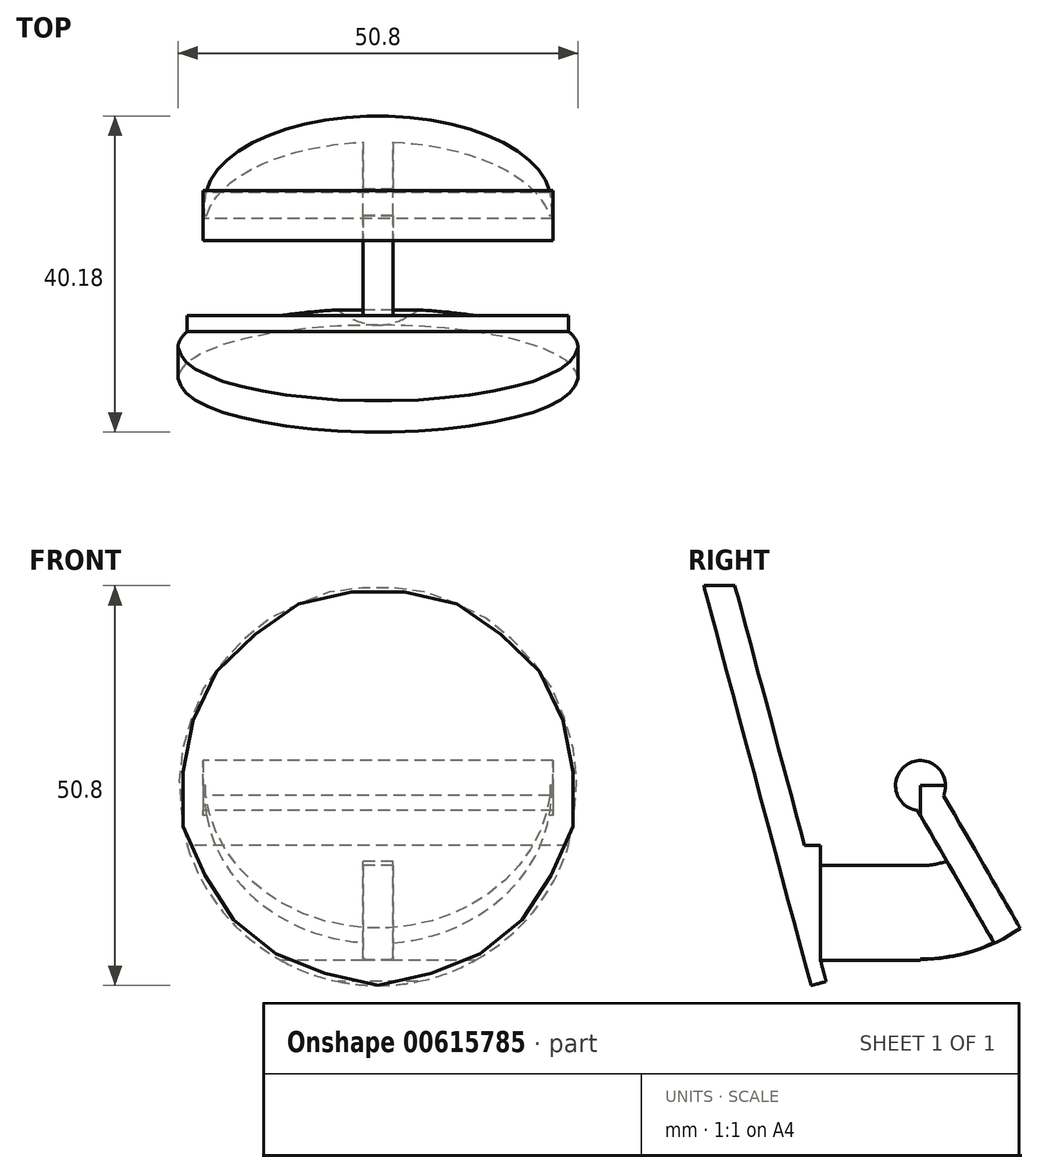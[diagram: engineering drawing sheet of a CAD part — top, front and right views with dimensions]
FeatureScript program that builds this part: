
annotation { "Feature Type Name" : "Feature", "Feature Type Description" : "" }
export const myFeature = defineFeature(function(context is Context, id is Id, definition is map)
    precondition{}
    {
        {
            var Q0;
            Q0=qCreatedBy(makeId("Right.planeOp"),FACE);
            var sketch = newSketch(context, id + "F0", { "sketchPlane" : qUnion([Q0])});
            skCircle(sketch, "E0", {"center": v(0, 0) * mm, "radius": 3.17 * mm});
            skLineSegment(sketch, "E1", {"start": v(2.92, -1.25) * mm, "end": v(28.32, -45.24) * mm});
            skLineSegment(sketch, "E2", {"start": v(28.32, -45.24) * mm, "end": v(25.02, -47.15) * mm});
            skLineSegment(sketch, "E3", {"start": v(25.02, -47.15) * mm, "end": v(-0.38, -3.15) * mm});
            skLineSegment(sketch, "E4", {"start": v(0, 0) * mm, "end": v(3.28, -5.69) * mm, "construction": true});
            skSolve(sketch);
        }
        {
            var Q0;
            Q0 = qSketchRegion(id + "F0", true);
            extrude(context, id + "F1", {"entities" : qUnion([Q0]), "endBound" : BoundingType.SYMMETRIC, "depth" : 44.45 * mm, "offsetDistance" : 25.4 * mm});
        }
        {
            var Q0;
            Q0=qCreatedBy(makeId("Right.planeOp"),FACE);
            var sketch = newSketch(context, id + "F2", { "sketchPlane" : qUnion([Q0])});
            skArc(sketch, "E5", {"start": v(4.9, -8.9) * mm, "mid": v(2.53, -9.84) * mm, "end": v(0, -10.16) * mm});
            skLineSegment(sketch, "E6", {"start": v(-12.7, 0) * mm, "end": v(-12.7, -23.65) * mm, "construction": true});
            skLineSegment(sketch, "E7", {"start": v(0, -10.16) * mm, "end": v(-12.7, -10.16) * mm});
            skLineSegment(sketch, "E8", {"start": v(-12.7, -10.16) * mm, "end": v(-12.7, -53.34) * mm});
            skLineSegment(sketch, "E9", {"start": v(-12.7, -53.34) * mm, "end": v(0, -53.34) * mm});
            skArc(sketch, "E10", {"start": v(0, -53.34) * mm, "mid": v(13.7, -51.55) * mm, "end": v(26.5, -46.3) * mm});
            skLineSegment(sketch, "E11", {"start": v(4.9, -8.9) * mm, "end": v(26.5, -46.3) * mm});
            skSolve(sketch);
        }
        {
            var Q0;
            Q0 = qSketchRegion(id + "F2", true);
            extrude(context, id + "F3", {"entities" : qUnion([Q0]), "operationType" : NewBodyOperationType.ADD, "endBound" : BoundingType.SYMMETRIC, "depth" : 3.8 * mm, "offsetDistance" : 25.4 * mm});
        }
        {
            var Q0;
            Q0=qCreatedBy(makeId("Right.planeOp"),FACE);
            var sketch = newSketch(context, id + "F4", { "sketchPlane" : qUnion([Q0])});
            skArc(sketch, "E12", {"start": v(0, -22.23) * mm, "mid": v(21.2, 6.66) * mm, "end": v(-12.7, 18.24) * mm});
            skLineSegment(sketch, "E13", {"start": v(0, -22.23) * mm, "end": v(-12.7, -22.23) * mm});
            skLineSegment(sketch, "E14", {"start": v(-12.7, -22.23) * mm, "end": v(-12.7, 18.24) * mm});
            skSolve(sketch);
        }
        {
            var Q0;
            Q0 = qSketchRegion(id + "F4", true);
            extrude(context, id + "F5", {"entities" : qUnion([Q0]), "operationType" : NewBodyOperationType.INTERSECT, "endBound" : BoundingType.SYMMETRIC, "depth" : 76.2 * mm, "offsetDistance" : 25.4 * mm});
        }
        {
            var Q0;
            Q0=qCreatedBy(makeId("Front.planeOp"),FACE);
            var sketch = newSketch(context, id + "F6", { "sketchPlane" : qUnion([Q0])});
            skLineSegment(sketch, "E15", {"start": v(18.5, -7.35) * mm, "end": v(18.5, -7.35) * mm});
            skLineSegment(sketch, "E16", {"start": v(0, 0) * mm, "end": v(22.1, 0) * mm, "construction": true});
            skArc(sketch, "E17", {"start": v(22.1, 0) * mm, "mid": v(0, -22.1) * mm, "end": v(-22.1, 0) * mm});
            skLineSegment(sketch, "E18", {"start": v(-22.1, 0) * mm, "end": v(0, 0) * mm, "construction": true});
            skLineSegment(sketch, "E19", {"start": v(-30.28, 0) * mm, "end": v(-30.28, -27.19) * mm});
            skLineSegment(sketch, "E20", {"start": v(-30.28, -27.19) * mm, "end": v(29.54, -27.19) * mm});
            skLineSegment(sketch, "E21", {"start": v(29.54, -27.19) * mm, "end": v(29.54, 0) * mm});
            skLineSegment(sketch, "E22", {"start": v(29.54, 0) * mm, "end": v(22.1, 0) * mm});
            skLineSegment(sketch, "E23", {"start": v(-22.1, 0) * mm, "end": v(-30.28, 0) * mm});
            skSolve(sketch);
        }
        {
            var Q0;
            Q0 = qSketchRegion(id + "F6", true);
            var Q1;
            Q1=sQuery(id+"F6.wireOp",EDGE,"E16");
            revolve(context, id + "F7", {"operationType" : NewBodyOperationType.REMOVE, "entities" : qUnion([Q0]), "axis" : qUnion([Q1]), "revolveType" : RevolveType.ONE_DIRECTION, "angle" : 90 * degree});
        }
        {
            var Q0;
            Q0=qCreatedBy(makeId("Right.planeOp"),FACE);
            var sketch = newSketch(context, id + "F8", { "sketchPlane" : qUnion([Q0])});
            skLineSegment(sketch, "E24", {"start": v(-27.52, 25.4) * mm, "end": v(-14.76, -22.23) * mm});
            skLineSegment(sketch, "E25", {"start": v(-14.76, -22.23) * mm, "end": v(-12.7, -22.23) * mm});
            skLineSegment(sketch, "E26", {"start": v(-12.7, -22.23) * mm, "end": v(-12.7, -7.62) * mm});
            skLineSegment(sketch, "E27", {"start": v(-12.7, -7.62) * mm, "end": v(-14.73, -7.62) * mm});
            skLineSegment(sketch, "E28", {"start": v(-14.73, -7.62) * mm, "end": v(-23.58, 25.4) * mm});
            skLineSegment(sketch, "E29", {"start": v(-23.58, 25.4) * mm, "end": v(-27.52, 25.4) * mm});
            skLineSegment(sketch, "E30", {"start": v(-14.76, -22.23) * mm, "end": v(-13.91, -25.4) * mm});
            skLineSegment(sketch, "E31", {"start": v(-13.91, -25.4) * mm, "end": v(-11.99, -24.88) * mm});
            skLineSegment(sketch, "E32", {"start": v(-11.99, -24.88) * mm, "end": v(-12.7, -22.23) * mm});
            skSolve(sketch);
        }
        {
            var Q0;
            Q0 = qSketchRegion(id + "F8", true);
            extrude(context, id + "F9", {"entities" : qUnion([Q0]), "operationType" : NewBodyOperationType.ADD, "endBound" : BoundingType.SYMMETRIC, "depth" : 63.5 * mm, "offsetDistance" : 25.4 * mm});
        }
        {
            var Q0;
            Q0=qCreatedBy(makeId("Front.planeOp"),FACE);
            var sketch = newSketch(context, id + "F10", { "sketchPlane" : qUnion([Q0])});
            skCircle(sketch, "E33", {"center": v(0, 0) * mm, "radius": 25.4 * mm});
            skSolve(sketch);
        }
        {
            var Q0;
            Q0 = qSketchRegion(id + "F10", true);
            extrude(context, id + "F11", {"entities" : qUnion([Q0]), "operationType" : NewBodyOperationType.INTERSECT, "endBound" : BoundingType.THROUGH_ALL, "oppositeDirection" : true, "depth" : 25.4 * mm, "offsetDistance" : 25.4 * mm, "hasSecondDirection" : true, "secondDirectionBound" : SecondDirectionBoundingType.THROUGH_ALL, "secondDirectionOppositeDirection" : false, "secondDirectionDepth" : 25.4 * mm});
        }
    });
